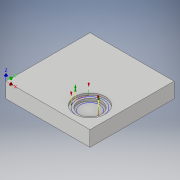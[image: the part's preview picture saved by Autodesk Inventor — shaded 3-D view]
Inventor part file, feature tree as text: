
AUTODESK INVENTOR PART (.ipt)
format: ipt  version: 2017 SP1 (Build 210196100, 196)  size: 241,664 bytes
history: native  units: in
note: dims shown in document units (in); Inventor stores cm internally (conversion verified against a paired STEP export)
features: extrude x3, sketch x3, projected_geometry x1
ambient origin geometry x8: Origin, YZ Plane, XZ Plane, XY Plane, X Axis, Y Axis, Z Axis, Center Point
bodies: Solid1 (feature_tree)
feature tree (7):
  extrude  "Extrusion1"  Depth=5.5in
  extrude  "Extrusion2"  Depth=1.0in
  extrude  "Extrusion3"  Depth=0.155in
  sketch  "Sketch1"  dims[d0=5.5in d1=5.5in]
  sketch  "Sketch2"  dims[d2=1.0in d3=0.0in d4=2.0in]
  projected_geometry  "Projected Loop1"
  sketch  "Sketch3"  dims[d5=1.375in d6=1.375in d7=0.125in d8=0.0in d9=1.5in d10=0.155in d11=0.0in]
